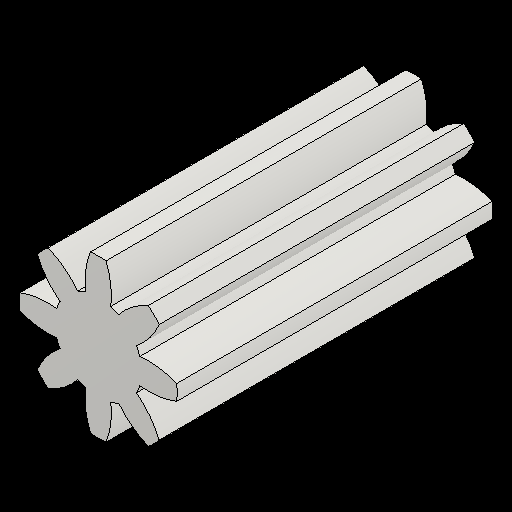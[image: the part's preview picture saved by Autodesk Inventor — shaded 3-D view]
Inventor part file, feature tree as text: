
AUTODESK INVENTOR PART (.ipt)
format: ipt  version: 2023.2 (Build 272271030, 271C)  size: 179,712 bytes
history: native  units: mm (DEFAULTED — no unit token found)
features: plane x3, other x3, sketch x2, extrude x1
ambient origin geometry x8: Origin, YZ Plane, XZ Plane, XY Plane, X Axis, Y Axis, Z Axis, Center Point
bodies: Solid1 (feature_tree)
feature tree (9):
  extrude  "Extrusion1"  Depth=20.0mm TaperAngle=0.0deg
  plane  "Work Plane2"
  plane  "Work Plane8"
  plane  "Work Plane9"
  other  "Spur Gear"
  sketch  "Sketch1"  dims[d0=10.0mm d1=20.0mm d2=0.0mm]
  sketch  "Sketch2"  dims[d3=8.0mm d4=10.0mm d5=0.0mm d16=12.0mm d17=0.0mm d34=22.5deg d39=0.0mm d41=0.0mm d43=12.0mm d46=12.0mm d47=0.0mm d48=0.0mm]
  other  "Srf1"
  other  "Pitch Diameter"
